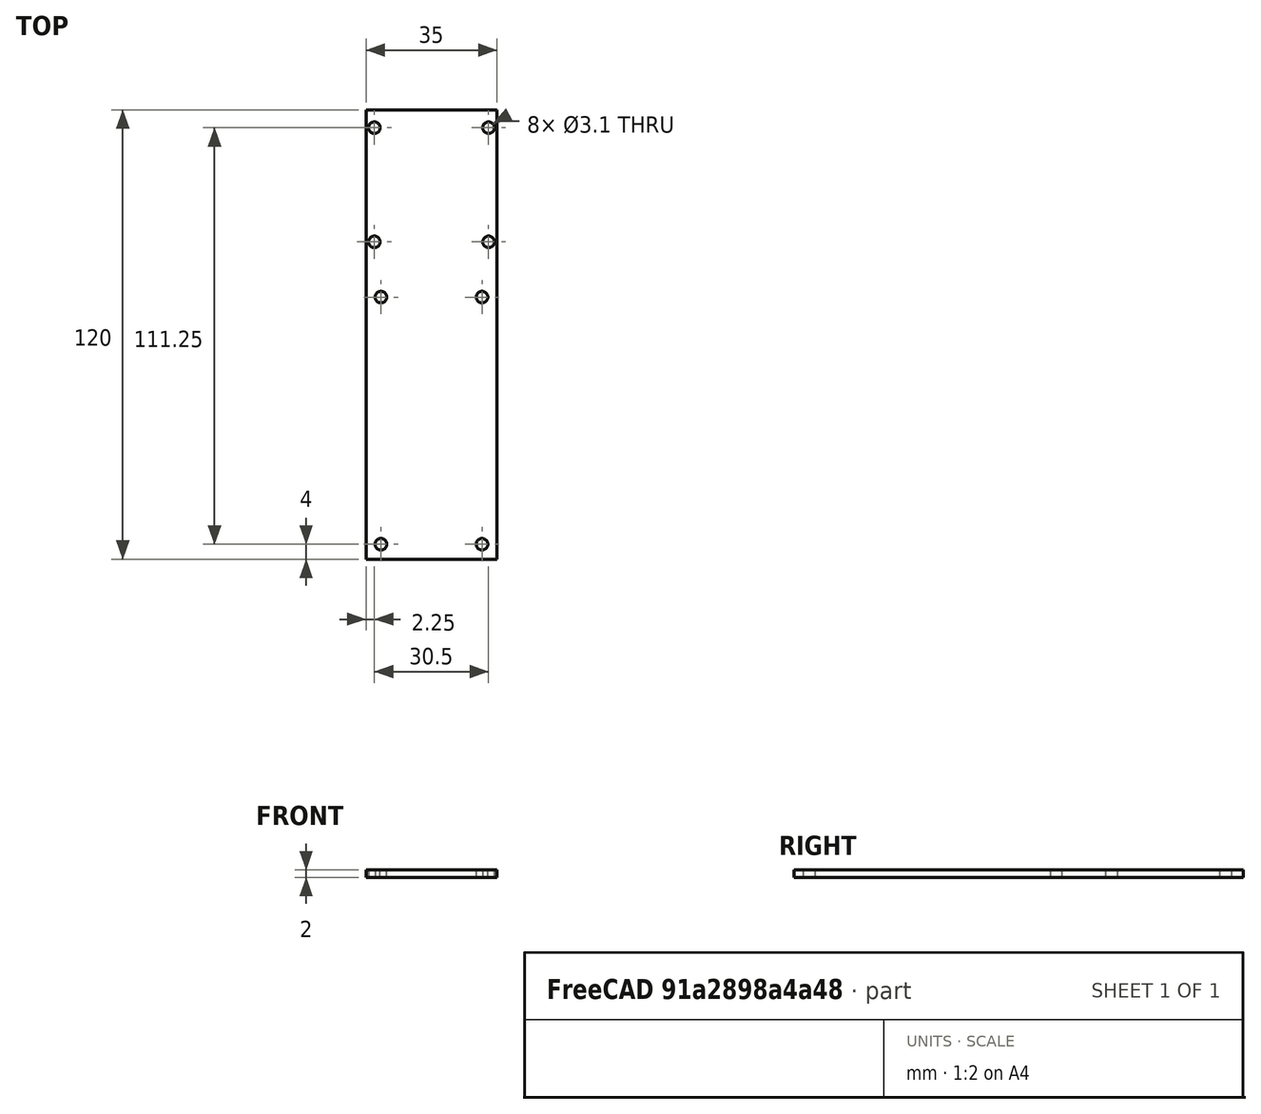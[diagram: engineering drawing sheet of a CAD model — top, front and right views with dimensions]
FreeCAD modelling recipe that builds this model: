
FCSTD DOCUMENT  (FreeCAD 0.20R29410 (Git))
Label: lower_plate
License: All rights reserved
LicenseURL: http://en.wikipedia.org/wiki/All_rights_reserved
objects: PartDesign::CoordinateSystem×9, Sketcher::SketchObject×1, PartDesign::Pad×1, PartDesign::Body×1
note: 13 computed .brp shape members not serialized (recipe doc carries the construction recipe); baked Part::Feature solids carry a one-line shape summary decoded from their .brp

FEATURE [Sketcher::SketchObject] Sketch
  FullyConstrained = true
  MapMode = 5
  Support = -> [XY_Plane]
  sketch-geometry (12):
    g0: LineSegment StartX=-17.5 StartY=20 StartZ=0 EndX=17.5 EndY=20 EndZ=0
    g1: LineSegment StartX=17.5 StartY=20 StartZ=0 EndX=17.5 EndY=-100 EndZ=0
    g2: LineSegment StartX=-17.5 StartY=-100 StartZ=0 EndX=-17.5 EndY=20 EndZ=0
    g3: Circle CenterX=-15.25 CenterY=15.25 CenterZ=0 NormalX=0 NormalY=0 NormalZ=1 AngleXU=0 Radius=1.55
    g4: Circle CenterX=15.25 CenterY=15.25 CenterZ=0 NormalX=0 NormalY=0 NormalZ=1 AngleXU=0 Radius=1.55
    g5: Circle CenterX=-15.25 CenterY=-15.25 CenterZ=0 NormalX=0 NormalY=0 NormalZ=1 AngleXU=0 Radius=1.55
    g6: Circle CenterX=15.25 CenterY=-15.25 CenterZ=0 NormalX=0 NormalY=0 NormalZ=1 AngleXU=0 Radius=1.55
    g7: LineSegment StartX=-17.5 StartY=-100 StartZ=0 EndX=17.5 EndY=-100 EndZ=0
    g8: Circle CenterX=-13.5 CenterY=-96 CenterZ=0 NormalX=0 NormalY=0 NormalZ=1 AngleXU=0 Radius=1.55
    g9: Circle CenterX=13.5 CenterY=-96 CenterZ=0 NormalX=0 NormalY=0 NormalZ=1 AngleXU=0 Radius=1.55
    g10: Circle CenterX=-13.5 CenterY=-30 CenterZ=0 NormalX=0 NormalY=0 NormalZ=1 AngleXU=0 Radius=1.55
    g11: Circle CenterX=13.5 CenterY=-30 CenterZ=0 NormalX=0 NormalY=0 NormalZ=1 AngleXU=0 Radius=1.55
  constraints (30):
    c: Coincident(g0,g1)
    c: Coincident(g2,g0)
    c: Vertical(g2)
    c: DistanceX(g2,g1) = 35
    c: Equal(g6,g5)
    c: Equal(g5,g3)
    c: Equal(g3,g4)
    c: Symmetric(g3,g4,g-2)
    c: Symmetric(g6,g4,g-1)
    c: Symmetric(g3,g5,g-1)
    c: DistanceX(g3,g4) = 30.5
    c: DistanceY(g6,g4) = 30.5
    c: Diameter(g6) = 3.1
    c: Vertical(g1)
    c: DistanceY(g-1,g0) = 20
    c: Symmetric(g0,g0,g-2)
    c: Equal(g2,g1)
    c: DistanceY(g1,g1) = 120
    c: Coincident(g7,g2)
    c: Coincident(g7,g1)
    c: Equal(g9,g8)
    c: Diameter(g9) = 3.1
    c: Symmetric(g8,g9,g-2)
    c: DistanceX(g9,g1) = 4
    c: DistanceY(g1,g9) = 4
    c: Equal(g11,g10)
    c: Symmetric(g11,g10,g-2)
    c: Diameter(g11) = 3.1
    c: DistanceX(g11,g1) = 4
    c: DistanceY(g1,g11) = 70
FEATURE [PartDesign::Pad] Pad
  Direction = (0,0,1)
  Length = 2
  Length2 = 10
  Profile = -> Sketch
  ReferenceAxis = -> Sketch [N_Axis]
  Type = 0
FEATURE [PartDesign::CoordinateSystem] LCS_1
  AttacherType = Attacher::AttachEngine3D
  MapMode = 1
  Placement = pos=(17.5,-100,0) rot=(0,0,1;0rad)
  Support = -> [Pad]
FEATURE [PartDesign::CoordinateSystem] LCS_2
  AttacherType = Attacher::AttachEngine3D
  MapMode = 11
  Placement = pos=(-15.25,-15.25,2) rot=(0,0,1;1.5708rad)
  Support = -> [Pad]
FEATURE [PartDesign::CoordinateSystem] LCS_3
  AttacherType = Attacher::AttachEngine3D
  MapMode = 11
  Placement = pos=(15.25,-15.25,2) rot=(0,0,1;1.5708rad)
  Support = -> [Pad]
FEATURE [PartDesign::CoordinateSystem] LCS_4
  AttacherType = Attacher::AttachEngine3D
  MapMode = 11
  Placement = pos=(-13.5,-96,2) rot=(0,0,1;1.5708rad)
  Support = -> [Pad]
FEATURE [PartDesign::CoordinateSystem] LCS_5
  AttacherType = Attacher::AttachEngine3D
  MapMode = 11
  Placement = pos=(13.5,-96,2) rot=(0,0,1;1.5708rad)
  Support = -> [Pad]
FEATURE [PartDesign::CoordinateSystem] LCS_6
  AttacherType = Attacher::AttachEngine3D
  MapMode = 11
  Placement = pos=(15.25,15.25,2) rot=(0,0,1;1.5708rad)
  Support = -> [Pad]
FEATURE [PartDesign::CoordinateSystem] LCS_7
  AttacherType = Attacher::AttachEngine3D
  MapMode = 11
  Placement = pos=(-15.25,15.25,2) rot=(0,0,1;1.5708rad)
  Support = -> [Pad]
FEATURE [PartDesign::CoordinateSystem] LCS_8
  AttacherType = Attacher::AttachEngine3D
  MapMode = 11
  Placement = pos=(-13.5,-30,2) rot=(0,0,1;1.5708rad)
  Support = -> [Pad]
FEATURE [PartDesign::CoordinateSystem] LCS_9
  AttacherType = Attacher::AttachEngine3D
  MapMode = 11
  Placement = pos=(13.5,-30,2) rot=(0,0,1;1.5708rad)
  Support = -> [Pad]
FEATURE [PartDesign::Body] Body
  Group = -> [Sketch,Pad,LCS_1,LCS_2,LCS_3,LCS_4,LCS_5,LCS_6,LCS_7,LCS_8,LCS_9]
  Origin = -> Origin
  Tip = -> Pad
